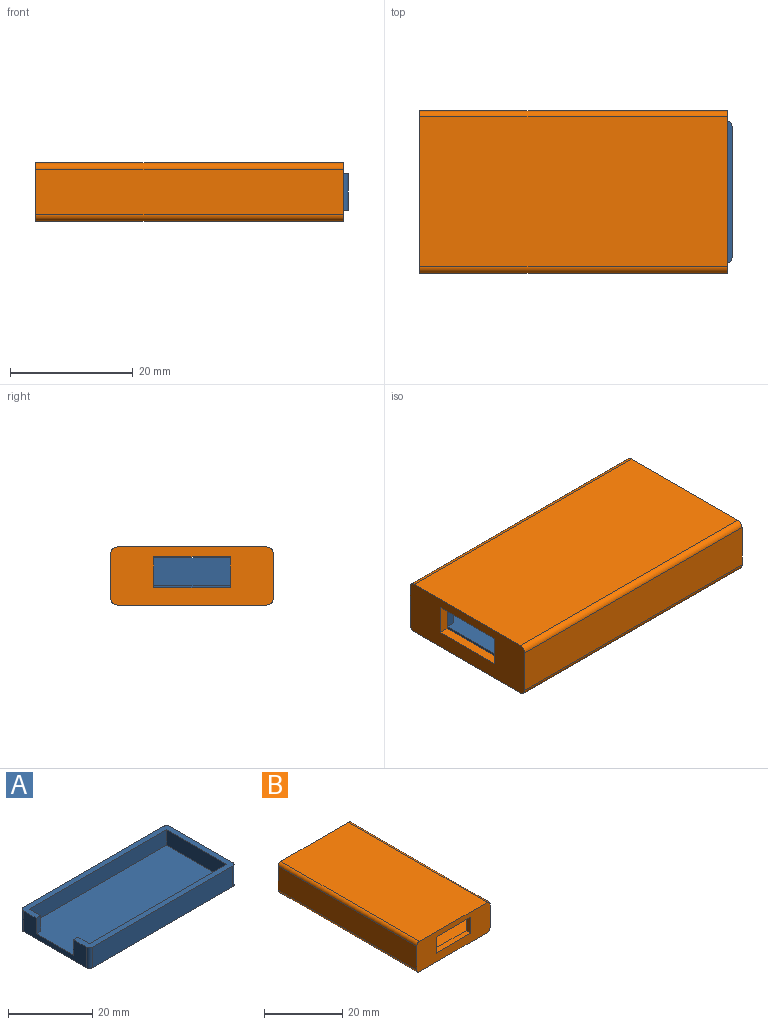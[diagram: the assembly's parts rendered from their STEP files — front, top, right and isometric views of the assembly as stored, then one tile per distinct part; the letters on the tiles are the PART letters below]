
ASSEMBLY  parts=2 mates=1
PART A: 18 faces, bbox 49.2x23.2x6 mm
  f0: plane 49.2x23.2mm, normal (0,0,1), area 188.6mm2, adj f1,f2,f3,f4,f5,f7,f8,f9
  f1: plane 4.5x3.85mm, normal (1,0,0), area 17.3mm2, adj f0,f7,f11,f12
  f2: plane 47.2x6mm, normal (0,1,0), area 283.2mm2, adj f0,f6,f14,f17
  f3: plane 21.2x6mm, normal (-1,0,0), area 70.9mm2, adj f0,f6,f11,f12,f13,f14,f15
  f4: plane 47.2x6mm, normal (0,-1,0), area 283.2mm2, adj f0,f6,f15,f16
  f5: plane 21.2x6mm, normal (1,0,0), area 127.2mm2, adj f0,f6,f16,f17
  f6: plane 49.2x23.2mm, normal (0,0,-1), area 1140.6mm2, adj f2,f3,f4,f5,f14,f15,f16,f17
  f7: plane 46.2x4.5mm, normal (0,-1,0), area 207.9mm2, adj f0,f1,f10,f11
  f8: plane 4.5x3.85mm, normal (1,0,0), area 17.3mm2, adj f0,f9,f11,f13
  f9: plane 46.2x4.5mm, normal (0,1,0), area 207.9mm2, adj f0,f8,f10,f11
  f10: plane 20.2x4.5mm, normal (-1,0,0), area 90.9mm2, adj f0,f7,f9,f11
  f11: plane 47.7x20.2mm, normal (0,0,1), area 952mm2, adj f1,f3,f7,f8,f9,f10,f12,f13
  f12: plane 4.5x1.5mm, normal (0,-1,0), area 6.8mm2, adj f0,f1,f3,f11
  f13: plane 4.5x1.5mm, normal (0,1,0), area 6.8mm2, adj f0,f3,f8,f11
  f14: cylinder r=1mm len=6mm, axis (0,0,1), area 9.4mm2, adj f0,f2,f3,f6
  f15: cylinder r=1mm len=6mm, axis (0,0,-1), area 9.4mm2, adj f0,f3,f4,f6
  f16: cylinder r=1mm len=6mm, axis (0,0,1), area 9.4mm2, adj f0,f4,f5,f6
  f17: cylinder r=1mm len=6mm, axis (0,0,-1), area 9.4mm2, adj f0,f2,f5,f6
PART B: 18 faces, bbox 26.4x50x9.5 mm
  f0: plane 26.4x9.45mm, normal (0,-1,0), area 186.1mm2, adj f3,f4,f5,f6,f8,f11,f12,f13
  f1: plane 23.2x6.25mm, normal (0,1,0), area 82.5mm2, adj f7,f8,f9,f10,f11,f12,f13
  f2: plane 26.4x9.45mm, normal (0,1,0), area 103.6mm2, adj f3,f4,f5,f6,f7,f8,f9,f10
  f3: plane 50x7.45mm, normal (1,0,0), area 372.5mm2, adj f0,f2,f14,f17
  f4: plane 50x24.4mm, normal (0,0,1), area 1220mm2, adj f0,f2,f14,f15
  f5: plane 50x7.45mm, normal (-1,0,0), area 372.5mm2, adj f0,f2,f15,f16
  f6: plane 50x24.4mm, normal (0,0,-1), area 1220mm2, adj f0,f2,f16,f17
  f7: plane 48.4x6.25mm, normal (-1,0,0), area 302.5mm2, adj f1,f2,f8,f10
  f8: plane 50x23.2mm, normal (0,0,-1), area 1142.9mm2, adj f0,f1,f2,f7,f9,f11,f12
  f9: plane 48.4x6.25mm, normal (1,0,0), area 302.5mm2, adj f1,f2,f8,f10
  f10: plane 48.4x23.2mm, normal (0,0,1), area 1122.9mm2, adj f1,f2,f7,f9
  f11: plane 5x1.6mm, normal (-1,0,0), area 8mm2, adj f0,f1,f8,f13
  f12: plane 5x1.6mm, normal (1,0,0), area 8mm2, adj f0,f1,f8,f13
  f13: plane 12.5x1.6mm, normal (0,0,1), area 20mm2, adj f0,f1,f11,f12
  f14: cylinder r=1mm len=50mm, axis (0,-1,0), area 78.5mm2, adj f0,f2,f3,f4
  f15: cylinder r=1mm len=50mm, axis (0,1,0), area 78.5mm2, adj f0,f2,f4,f5
  f16: cylinder r=1mm len=50mm, axis (0,-1,0), area 78.5mm2, adj f0,f2,f5,f6
  f17: cylinder r=1mm len=50mm, axis (0,1,0), area 78.5mm2, adj f0,f2,f3,f6
PLACE A t=(-15.3,0,0)mm
PLACE B rot(axis=(0,0,-1),90deg) t=(8.5,0,3)mm
MATE slider B.f9 <-> A.f2  axis (0,-1,0) through (8.5,11.6,3)mm
